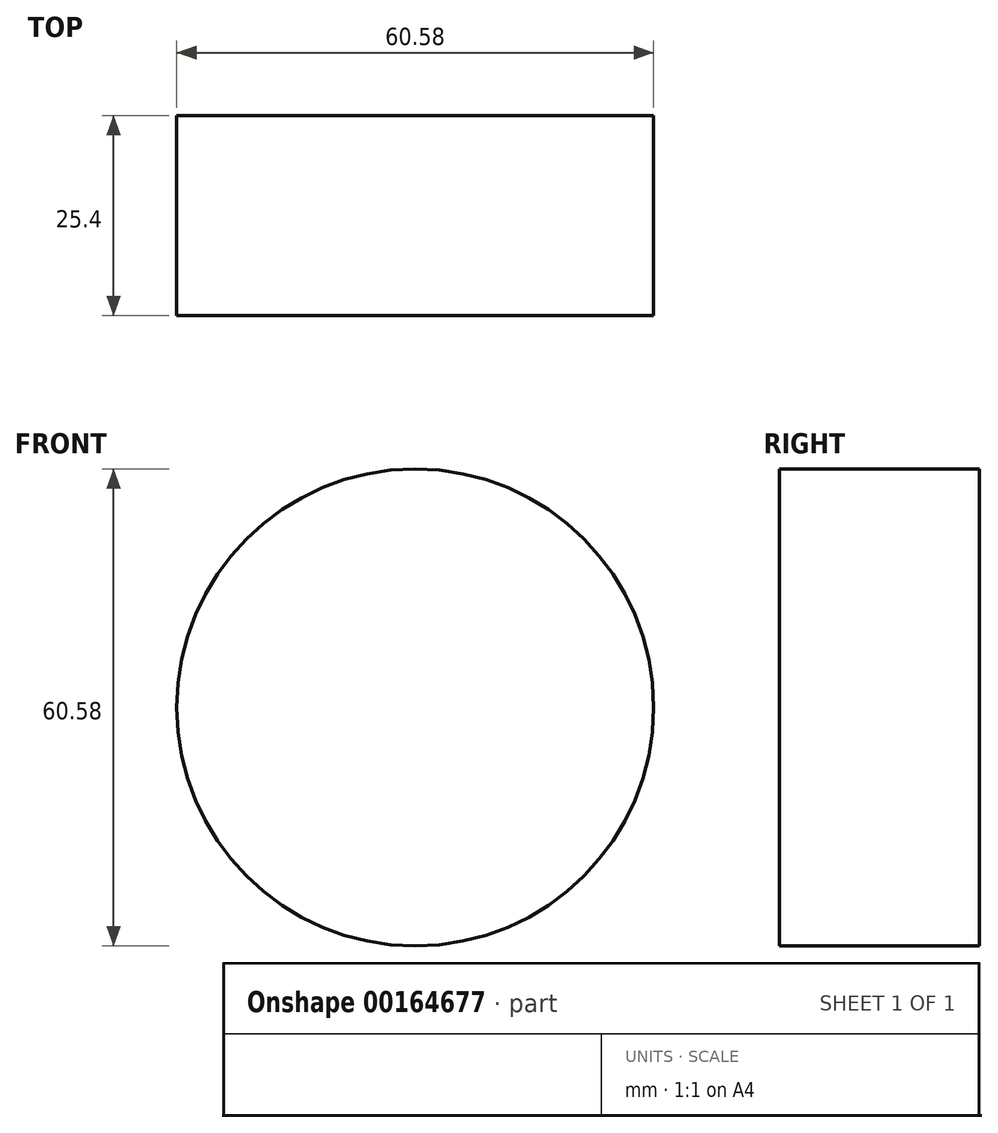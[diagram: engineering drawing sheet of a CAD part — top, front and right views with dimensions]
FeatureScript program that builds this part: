
annotation { "Feature Type Name" : "Feature", "Feature Type Description" : "" }
export const myFeature = defineFeature(function(context is Context, id is Id, definition is map)
    precondition{}
    {
        {
            var Q0;
            Q0=qCreatedBy(makeId("Front.planeOp"),FACE);
            var sketch = newSketch(context, id + "F0", { "sketchPlane" : qUnion([Q0])});
            skCircle(sketch, "E0", {"center": v(0, 0) * mm, "radius": 30.3 * mm});
            skSolve(sketch);
        }
        {
            var Q0;
            Q0 = qSketchRegion(id + "F0", true);
            extrude(context, id + "F1", {"entities" : qUnion([Q0]), "depth" : 25.4 * mm});
        }
    });
